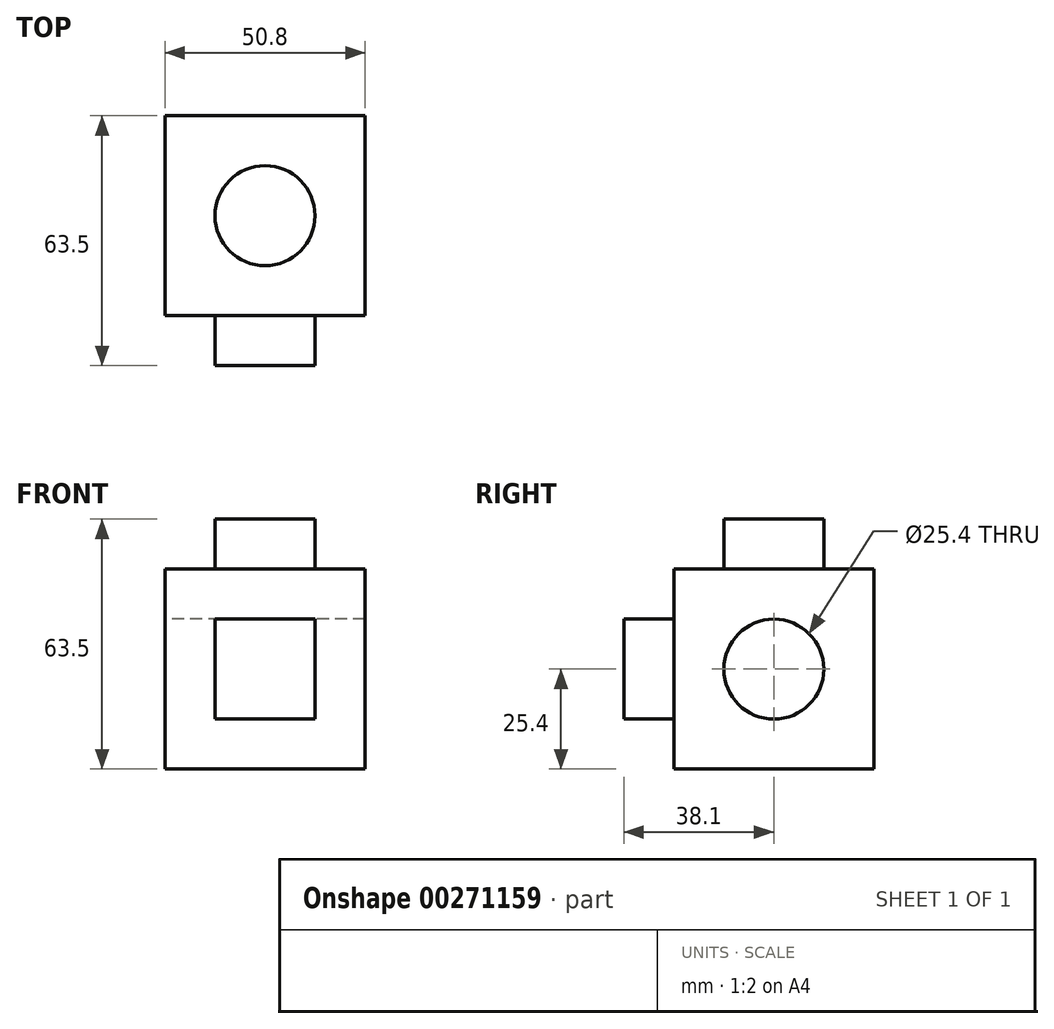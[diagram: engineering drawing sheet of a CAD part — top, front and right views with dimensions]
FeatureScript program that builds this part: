
annotation { "Feature Type Name" : "Feature", "Feature Type Description" : "" }
export const myFeature = defineFeature(function(context is Context, id is Id, definition is map)
    precondition{}
    {
        {
            var Q0;
            Q0=qCreatedBy(makeId("Front.planeOp"),FACE);
            var sketch = newSketch(context, id + "F0", { "sketchPlane" : qUnion([Q0])});
            skLineSegment(sketch, "E0.bottom", {"start": v(0, 0) * mm, "end": v(-50.8, 0) * mm});
            skLineSegment(sketch, "E0.top", {"start": v(0, 50.8) * mm, "end": v(-50.8, 50.8) * mm});
            skLineSegment(sketch, "E0.left", {"start": v(0, 0) * mm, "end": v(0, 50.8) * mm});
            skLineSegment(sketch, "E0.right", {"start": v(-50.8, 0) * mm, "end": v(-50.8, 50.8) * mm});
            skSolve(sketch);
        }
        {
            var Q0;
            Q0=makeQuery(id+"F0.imprint","IMPRINT",FACE,{"disambiguationData":[TD([[makeQuery(id+"F0.imprint","IMPRINT",EDGE,{"derivedFrom":sQuery(id+"F0.wireOp",EDGE,"E0.bottom")}),-1.0]])]});
            extrude(context, id + "F1", {"entities" : qUnion([Q0]), "depth" : 50.8 * mm});
        }
        {
            var Q0;
            Q0=makeQuery(id+"F1.opExtrude","CAP_FACE",FACE,{"disambiguationData":[OSD([sQuery(id+"F0.wireOp",EDGE,"E0.bottom"),sQuery(id+"F0.wireOp",EDGE,"E0.top"),sQuery(id+"F0.wireOp",EDGE,"E0.left"),sQuery(id+"F0.wireOp",EDGE,"E0.right")])],"isStart":false});
            var sketch = newSketch(context, id + "F2", { "sketchPlane" : qUnion([Q0])});
            skLineSegment(sketch, "E1.bottom", {"start": v(-12.7, 12.7) * mm, "end": v(-38.1, 12.7) * mm});
            skLineSegment(sketch, "E1.top", {"start": v(-12.7, 38.1) * mm, "end": v(-38.1, 38.1) * mm});
            skLineSegment(sketch, "E1.left", {"start": v(-12.7, 12.7) * mm, "end": v(-12.7, 38.1) * mm});
            skLineSegment(sketch, "E1.right", {"start": v(-38.1, 12.7) * mm, "end": v(-38.1, 38.1) * mm});
            skSolve(sketch);
        }
        {
            var Q0;
            Q0=makeQuery(id+"F2.imprint","IMPRINT",FACE,{"disambiguationData":[TD([[makeQuery(id+"F2.imprint","IMPRINT",EDGE,{"derivedFrom":sQuery(id+"F2.wireOp",EDGE,"E1.bottom")}),-1.0]])]});
            extrude(context, id + "F3", {"entities" : qUnion([Q0]), "operationType" : NewBodyOperationType.ADD, "depth" : 12.7 * mm});
        }
        {
            var Q0;
            Q0=makeQuery(id+"F1.opExtrude","SWEPT_FACE",FACE,{"disambiguationData":[OSD([sQuery(id+"F0.wireOp",EDGE,"E0.right")])]});
            var sketch = newSketch(context, id + "F4", { "sketchPlane" : qUnion([Q0])});
            skCircle(sketch, "E2", {"center": v(25.4, 25.4) * mm, "radius": 12.7 * mm});
            skSolve(sketch);
        }
        {
            var Q0;
            Q0 = qSketchRegion(id + "F4", true);
            var Q1;
            Q1=makeQuery(id+"F1.opExtrude","SWEPT_FACE",FACE,{"disambiguationData":[OSD([sQuery(id+"F0.wireOp",EDGE,"E0.left")])]});
            extrude(context, id + "F5", {"entities" : qUnion([Q0, Q1]), "operationType" : NewBodyOperationType.REMOVE, "oppositeDirection" : true, "depth" : 50.8 * mm});
        }
        {
            var Q0;
            Q0=makeQuery(id+"F1.opExtrude","SWEPT_FACE",FACE,{"disambiguationData":[OSD([sQuery(id+"F0.wireOp",EDGE,"E0.top")])]});
            var sketch = newSketch(context, id + "F6", { "sketchPlane" : qUnion([Q0])});
            skCircle(sketch, "E3", {"center": v(-25.4, -25.4) * mm, "radius": 12.7 * mm});
            skSolve(sketch);
        }
        {
            var Q0;
            Q0=makeQuery(id+"F6.imprint","IMPRINT",FACE,{"disambiguationData":[TD([[makeQuery(id+"F6.imprint","IMPRINT",EDGE,{"derivedFrom":sQuery(id+"F6.wireOp",EDGE,"E3")}),1.0]])]});
            extrude(context, id + "F7", {"entities" : qUnion([Q0]), "operationType" : NewBodyOperationType.ADD, "depth" : 12.7 * mm});
        }
    });
